# Revit family: Furniture-Console_Table_Top-KALLISTA-Per_Se-P74061
name_source: partatom
category: Specialty Equipment
units: mm (PartAtom-declared; Revit-internal decimal feet)

## family parameters
Cut with Voids When Loaded = No
Host = Face
Maintain Annotation Orientation = No
OmniClass Number = 23.31.25.00
OmniClass Title = Toilet and Bath Specialties
Part Type = Normal
Room Calculation Point = No
Round Connector Dimension = Use Diameter
Shared = No

## types (1)
- NM-Nero Marouina
    ADA Compliant = No
    Assembly Code = C1030200
    Date Modified = 06/29/2025
    Default Elevation = 42"
    Description = Console Table Top
    Finish = Kallista-Stone-NM-Nero_Marouina
    Height = 1 3/16"
    Length = 32"
    Manufacturer = Kallista Co.
    Master Format 2014 = 10 28 00
    Master Format 2014 Name = Toilet, Bath, and Laundry Accessories
    Material = Marble
    Model = P74061-00-NM
    Product Documentation Link = https://techcomm.kohler.com
    Product Name = Per Se
    Product Page URL = https://www.kallista.com
    Type = 1
    URL = https://www.kallista.com
    WaterSense Certified = No
    Width = 22"

## geometry (parser evidence)
native form markers: Sweep x5
no freeform markers — native parametric forms only
